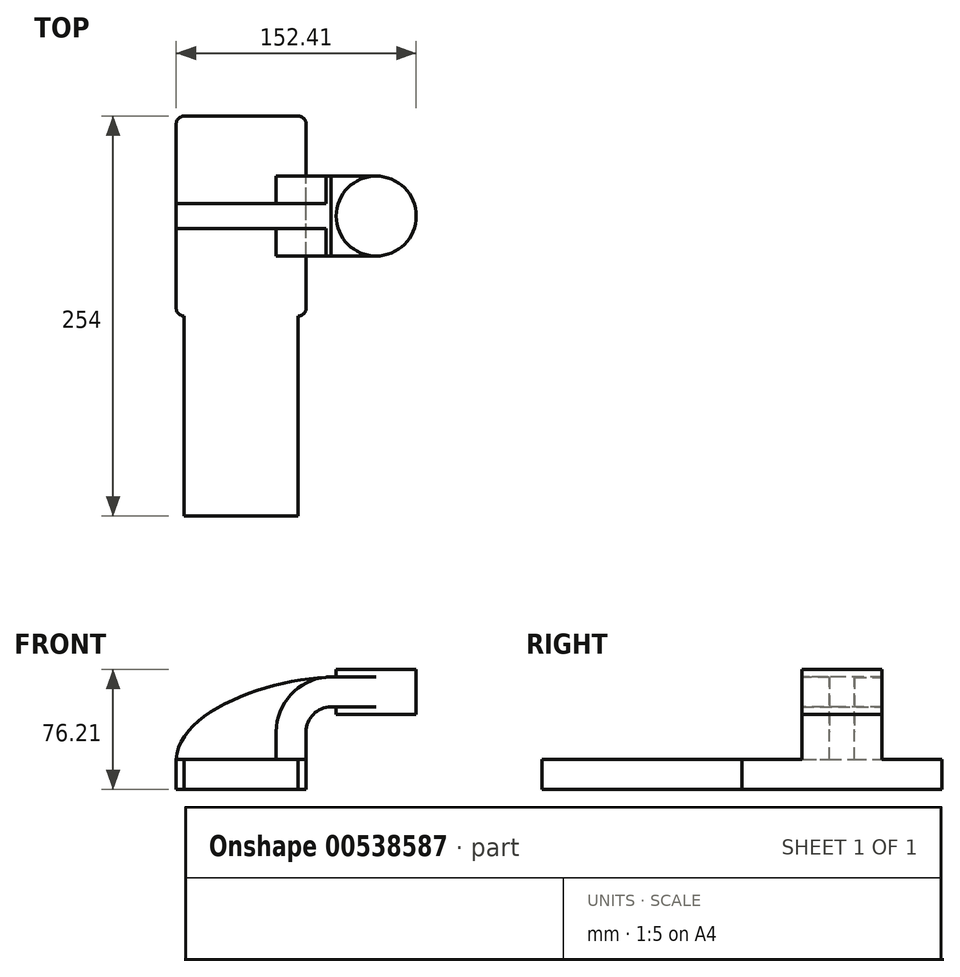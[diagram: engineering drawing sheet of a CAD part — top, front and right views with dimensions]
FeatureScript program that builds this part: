
annotation { "Feature Type Name" : "Feature", "Feature Type Description" : "" }
export const myFeature = defineFeature(function(context is Context, id is Id, definition is map)
    precondition{}
    {
        {
            var Q0;
            Q0=qCreatedBy(makeId("Front.planeOp"),FACE);
            var sketch = newSketch(context, id + "F0", { "sketchPlane" : qUnion([Q0])});
            skLineSegment(sketch, "E0.rect.bottom", {"start": v(-41.28, 9.52) * mm, "end": v(41.28, 9.52) * mm});
            skLineSegment(sketch, "E0.rect.top", {"start": v(-41.28, -9.52) * mm, "end": v(41.28, -9.52) * mm});
            skLineSegment(sketch, "E0.rect.left", {"start": v(-41.28, 9.52) * mm, "end": v(-41.28, -9.52) * mm});
            skLineSegment(sketch, "E0.rect.right", {"start": v(41.28, 9.52) * mm, "end": v(41.28, -9.52) * mm});
            skPoint(sketch, "E0.rect.middle", {"position": v(0, 0) * mm});
            skLineSegment(sketch, "E1", {"start": v(41.28, 9.52) * mm, "end": v(41.28, 27) * mm});
            skArc(sketch, "E2", {"start": v(41.28, 27) * mm, "mid": v(45.92, 38.23) * mm, "end": v(57.15, 42.88) * mm});
            skLineSegment(sketch, "E3", {"start": v(57.15, 42.88) * mm, "end": v(85.72, 42.88) * mm});
            skLineSegment(sketch, "E4.rect.bottom", {"start": v(60.32, 38.1) * mm, "end": v(111.12, 38.1) * mm});
            skLineSegment(sketch, "E4.rect.top", {"start": v(60.32, 66.68) * mm, "end": v(111.12, 66.68) * mm});
            skLineSegment(sketch, "E4.rect.left", {"start": v(60.32, 38.1) * mm, "end": v(60.32, 66.68) * mm});
            skLineSegment(sketch, "E4.rect.right", {"start": v(111.13, 38.1) * mm, "end": v(111.12, 66.68) * mm});
            skPoint(sketch, "E4.rect.middle", {"position": v(85.72, 52.39) * mm});
            skLineSegment(sketch, "E5.0", {"start": v(57.15, 61.93) * mm, "end": v(85.72, 61.93) * mm});
            skArc(sketch, "E5.1", {"start": v(22.23, 27) * mm, "mid": v(32.45, 51.7) * mm, "end": v(57.15, 61.93) * mm});
            skLineSegment(sketch, "E5.2", {"start": v(22.23, 9.52) * mm, "end": v(22.23, 27) * mm});
            skLineSegment(sketch, "E6", {"start": v(85.72, 38.1) * mm, "end": v(85.72, 66.68) * mm});
            skFitSpline(sketch, "E7", {"points": [v(-41.28, 9.53) * mm, v(57.15, 61.93) * mm], "startDerivative": vector(5.2, 92.34) * mm, "endDerivative": vector(120.92, 4.22) * mm});
            skSolve(sketch);
        }
        {
            var Q0;
            Q0=makeQuery(id+"F0.imprint","IMPRINT",FACE,{"disambiguationData":[TD([[makeQuery(id+"F0.imprint","IMPRINT",EDGE,{"derivedFrom":sQuery(id+"F0.wireOp",EDGE,"E0.rect.top")}),1.0]])]});
            extrude(context, id + "F1", {"entities" : qUnion([Q0]), "endBound" : BoundingType.SYMMETRIC, "depth" : 127 * mm});
        }
        {
            var Q0;
            {var subQ9=sQuery(id+"F0.wireOp",EDGE,"E1");Q0=makeQuery(id+"F0.imprint","IMPRINT",FACE,{"disambiguationData":[TD([[makeQuery(id+"F0.imprint","IMPRINT",EDGE,{"derivedFrom":subQ9}),1.0]])]});}
            var Q1;
            {var subQ0=sQuery(id+"F0.wireOp",EDGE,"E6");var subQ1=sQuery(id+"F0.wireOp",EDGE,"E3");var subQ2=makeQuery(id+"F0.imprint","INTERSECT",VERTEX,{"derivedFrom":[subQ1,subQ0]});Q1=makeQuery(id+"F0.imprint","IMPRINT",FACE,{"disambiguationData":[TD([[makeQuery(id+"F0.imprint","IMPRINT",EDGE,{"disambiguationData":[TD([[subQ2,1.0]])],"derivedFrom":subQ1}),1.0]])]});}
            extrude(context, id + "F2", {"entities" : qUnion([Q0, Q1]), "operationType" : NewBodyOperationType.ADD, "endBound" : BoundingType.SYMMETRIC, "depth" : 50.8 * mm});
        }
        {
            var Q0;
            {var subQ3=sQuery(id+"F0.wireOp",EDGE,"E5.2");Q0=makeQuery(id+"F0.imprint","IMPRINT",FACE,{"disambiguationData":[TD([[makeQuery(id+"F0.imprint","IMPRINT",EDGE,{"derivedFrom":subQ3}),1.0]])]});}
            extrude(context, id + "F3", {"entities" : qUnion([Q0]), "operationType" : NewBodyOperationType.ADD, "endBound" : BoundingType.SYMMETRIC, "depth" : 15.88 * mm});
        }
        {
            var Q0;
            {var subQ5=sQuery(id+"F0.wireOp",EDGE,"E4.rect.right");Q0=makeQuery(id+"F0.imprint","IMPRINT",FACE,{"disambiguationData":[TD([[makeQuery(id+"F0.imprint","IMPRINT",EDGE,{"derivedFrom":subQ5}),1.0]])]});}
            var Q1;
            Q1=sQuery(id+"F0.wireOp",EDGE,"E6");
            revolve(context, id + "F4", {"operationType" : NewBodyOperationType.ADD, "entities" : qUnion([Q0]), "axis" : qUnion([Q1]), "revolveType" : RevolveType.FULL});
        }
        {
            var Q0;
            Q0=makeQuery(id+"F1.opExtrude","CAP_EDGE",EDGE,{"disambiguationData":[OSD([sQuery(id+"F0.wireOp",EDGE,"E0.rect.right")])],"isStart":false});
            var Q1;
            Q1=makeQuery(id+"F1.opExtrude","CAP_EDGE",EDGE,{"disambiguationData":[OSD([sQuery(id+"F0.wireOp",EDGE,"E0.rect.left")])],"isStart":false});
            var Q2;
            Q2=makeQuery(id+"F1.opExtrude","CAP_EDGE",EDGE,{"disambiguationData":[OSD([sQuery(id+"F0.wireOp",EDGE,"E0.rect.right")])],"isStart":true});
            var Q3;
            Q3=makeQuery(id+"F1.opExtrude","CAP_EDGE",EDGE,{"disambiguationData":[OSD([sQuery(id+"F0.wireOp",EDGE,"E0.rect.left")])],"isStart":true});
            fillet(context, id + "F5", {"entities" : qUnion([Q0, Q1, Q2, Q3]), "radius" : 5.08 * mm, "tangentPropagation" : true, "allowEdgeOverflow" : false});
        }
        {
            var Q0;
            Q0=makeQuery(id+"F1.opExtrude","CAP_FACE",FACE,{"disambiguationData":[OSD([sQuery(id+"F0.wireOp",EDGE,"E0.rect.bottom"),sQuery(id+"F0.wireOp",EDGE,"E0.rect.top"),sQuery(id+"F0.wireOp",EDGE,"E0.rect.left"),sQuery(id+"F0.wireOp",EDGE,"E0.rect.right")])],"isStart":false});
            extrude(context, id + "F6", {"entities" : qUnion([Q0]), "operationType" : NewBodyOperationType.ADD, "depth" : 127 * mm, "offsetDistance" : 25.4 * mm});
        }
    });
